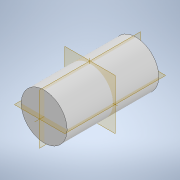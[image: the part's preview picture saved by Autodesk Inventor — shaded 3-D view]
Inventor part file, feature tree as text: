
AUTODESK INVENTOR PART (.ipt)
format: ipt  version: 2022.4 (Build 264492010, 492A)  size: 94,720 bytes
history: native  units: mm
features: extrude x1, sketch x1
ambient origin geometry x8: Origin, YZ Plane, XZ Plane, XY Plane, X Axis, Y Axis, Z Axis, Center Point
bodies: Solid1 (feature_tree)
feature tree (2):
  extrude  "Extrusion1"  Depth=10.0mm TaperAngle=0.0deg
  sketch  "Sketch1"  dims[d0=5.0mm d1=10.0mm d2=0.0mm]
